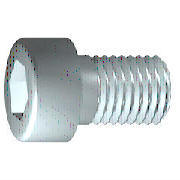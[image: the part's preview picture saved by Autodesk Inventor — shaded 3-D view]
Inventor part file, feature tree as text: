
AUTODESK INVENTOR PART (.ipt)
format: ipt  version: 2015 SP1 (Build 190203100, 203)  size: 193,024 bytes
history: native  units: mm (DEFAULTED — no unit token found)
features: sketch x2, extrude x1, plane x1, fillet x1
ambient origin geometry x7: Origin, YZ Plane, XY Plane, X Axis, Y Axis, Z Axis, Center Point
bodies: Solid1 (feature_tree), Body (feature_tree)
feature tree (5):
  extrude  "Slot"  Depth=3.0mm
  plane  "Work Plane1"
  fillet  "Fillet2"  Radius=3.0mm
  sketch  "Sketch1"  dims[d1=10.75mm d2=0.306825mm d3=3.0mm]
  sketch  "Sketch2"  dims[d4=1.3mm d5=60.0deg d6=3.0mm d7=3.0mm d8=2.886751mm d9=5.5mm d10=90.0deg d11=10.0mm d12=0.0mm d13=10.75mm d14=0.0mm d15=0.306725mm d16=0.306725mm d17=0.3mm d19=0.0mm d26=15.0mm d27=45.0deg d28=0.0mm d29=0.0mm d30=0.1mm]
